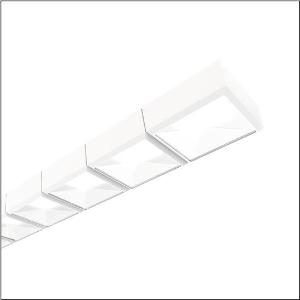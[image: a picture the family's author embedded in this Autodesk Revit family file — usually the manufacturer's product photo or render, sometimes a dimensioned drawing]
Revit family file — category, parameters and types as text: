
# Revit family: scriptus_11_5mz214d0twa
name_source: partatom
category: Lighting Fixtures
units: mm (PartAtom-declared; Revit-internal decimal feet)

## family parameters
Cut with Voids When Loaded = No
Host = Face
Light Source = No
Part Type = Normal
Room Calculation Point = No
Round Connector Dimension = Use Diameter
Shared = No

## types (1)
- --- (1 x LED 3000K+6500K / CRI = 80 (unbekannt), 3600 lm, 3000K)
    Apparent Load = 53 VA
    CIE Flux Codes = 82 95 99 100 100
    Color Rendering = 80
    Color Temperature = 3000K
    Default Elevation = 1800 mm
    Description = Scriptus 11, office luminaire, primary optical cover: lenses, CAT 2 (L<= 3000cd/m²), light emission: direct distribution, primary light characteristic: symmetric, installation type: surface-mounted, LED, rated luminous flux: 7.190lm, luminous efficacy: 137lm/W, light colour: 8tw, colour temperature: 3000..6500K, control gear: DALI, with terminal, 5-pole, mains connection: 230V, AC, 50Hz, rated input power: 53W, housing, luminaire housing, of aluminium, traffic white (RAL 9016), length: 3.088mm, width: 114mm, height: 57mm, protection rating (complete): IP20, insulation class (complete): insulation class I (protective earthing), certification: CE, protection symbol: F, permissible operating ambient temperature: 0..+35°C, standard: EN 50419, packaging unit: 1 piece
    Height = 57 mm
    Lamp = 1 x LED 3000K+6500K / CRI >= 80 (unbekannt)
    Lamp Light Flux = 3600 lm
    Lamp count = 1
    Length = 3088 mm
    Luminous efficacy = 137 lm/W
    Manufacturer = Siteco
    ModVariant = No
    Model = 5MZ214D0TWA
    Mounting Place = Ceiling
    Mounting Type = Surface mounted
    Number of Poles = 1
    OnlyDefault = Yes
    Power Factor = 1
    Product Name = Scriptus 11
    Product group = office luminaire | ceiling mounted
    ProductGroupID = 301
    Protection Class = Protection class I
    Protection Degree = IP 20
    RLX_Detail_Level = 1
    RLX_Emergency_Light_Flux = 0 lm
    RLX_Emergency_Type = 0
    RLX_Emergency_Type_DB = No
    RlxData = <blob elided: 30405 chars, md5=f165f969>
    Socket = socket
    Standby Power = 0 W
    System Light Flux = 7200 lm
    System Power = 53 W
    Type Comments = individual setting: colour temperature 6500K
    Type Image = l_1004833.jpg
    URL = http://relux.com
    VarID = @adj_197839
    Voltage = 0 V
    Weight = 0.00 kg
    Width = 114 mm

## geometry (parser evidence)
native form markers: Blend x4, Sweep x17
no freeform markers — native parametric forms only
